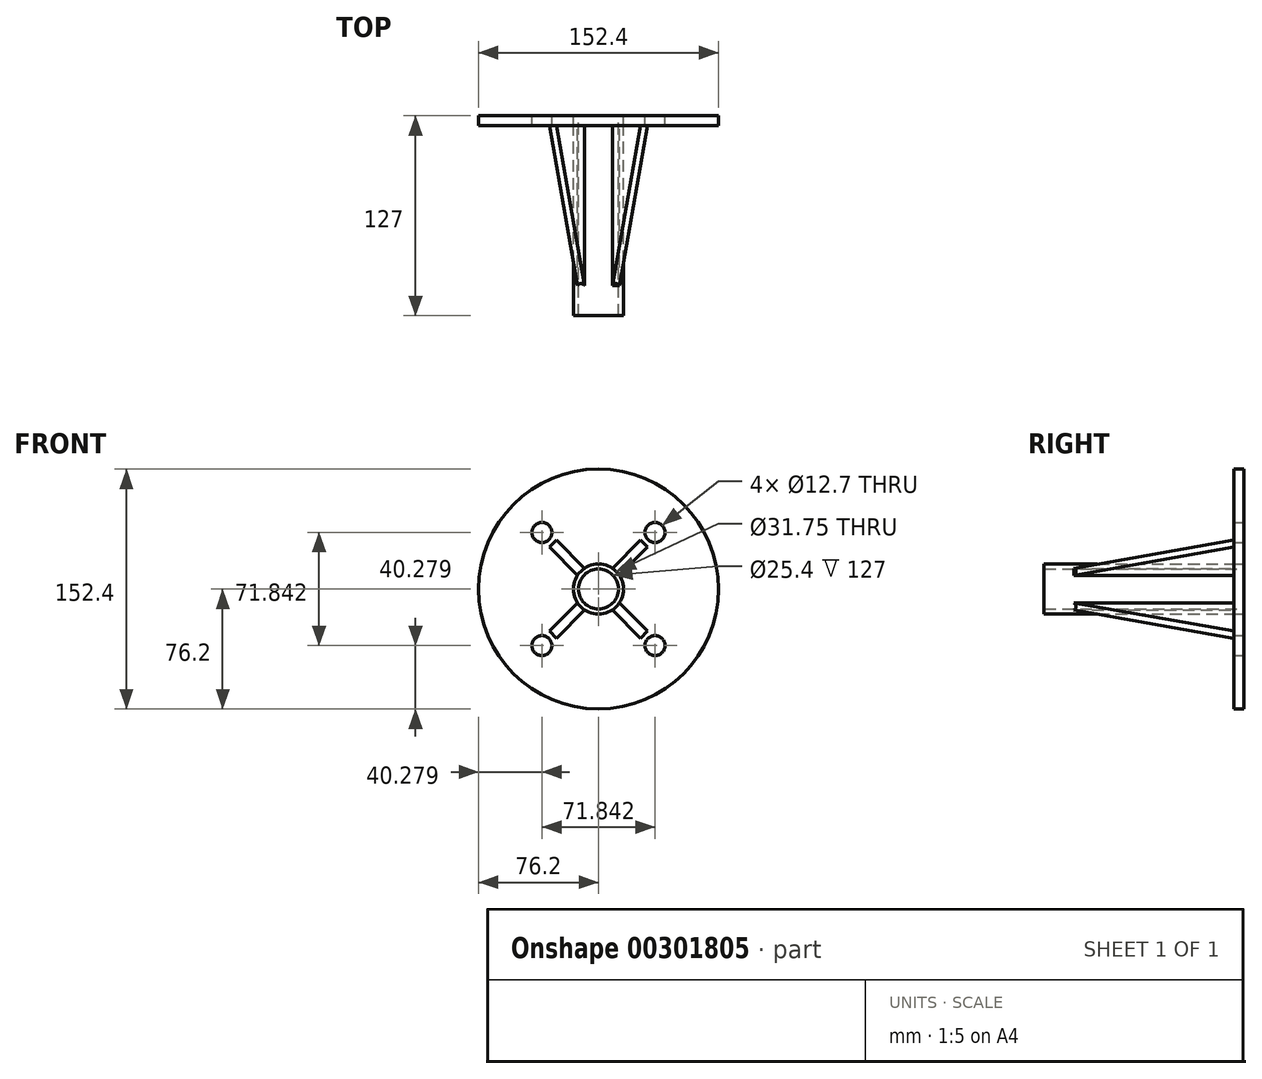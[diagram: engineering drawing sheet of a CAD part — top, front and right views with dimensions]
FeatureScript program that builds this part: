
annotation { "Feature Type Name" : "Feature", "Feature Type Description" : "" }
export const myFeature = defineFeature(function(context is Context, id is Id, definition is map)
    precondition{}
    {
        {
            var Q0;
            Q0=qCreatedBy(makeId("Front.planeOp"),FACE);
            var sketch = newSketch(context, id + "F0", { "sketchPlane" : qUnion([Q0])});
            skCircle(sketch, "E0", {"center": v(0, 0) * mm, "radius": 12.7 * mm});
            skCircle(sketch, "E1", {"center": v(0, 0) * mm, "radius": 15.88 * mm});
            skSolve(sketch);
        }
        {
            var Q0;
            Q0=makeQuery(id+"F0.imprint","IMPRINT",FACE,{"disambiguationData":[TD([[makeQuery(id+"F0.imprint","IMPRINT",EDGE,{"derivedFrom":sQuery(id+"F0.wireOp",EDGE,"E0")}),-1.0]])]});
            extrude(context, id + "F1", {"entities" : qUnion([Q0]), "depth" : 127 * mm});
        }
        {
            var Q0;
            Q0=qCreatedBy(makeId("Front.planeOp"),FACE);
            var sketch = newSketch(context, id + "F2", { "sketchPlane" : qUnion([Q0])});
            skCircle(sketch, "E2", {"center": v(0, 0) * mm, "radius": 15.88 * mm});
            skCircle(sketch, "E3", {"center": v(0, 0) * mm, "radius": 76.2 * mm});
            skCircle(sketch, "E4", {"center": v(-35.92, 35.92) * mm, "radius": 6.35 * mm});
            skLineSegment(sketch, "E5", {"start": v(0, -180.48) * mm, "end": v(0, 180.48) * mm, "construction": true});
            skLineSegment(sketch, "E6", {"start": v(169.83, 0) * mm, "end": v(-169.83, 0) * mm, "construction": true});
            skCircle(sketch, "E7.MirrorC", {"center": v(35.92, 35.92) * mm, "radius": 6.35 * mm});
            skCircle(sketch, "E8.MirrorC", {"center": v(-35.92, -35.92) * mm, "radius": 6.35 * mm});
            skCircle(sketch, "E9.MirrorC", {"center": v(35.92, -35.92) * mm, "radius": 6.35 * mm});
            skLineSegment(sketch, "E10", {"start": v(0, 0) * mm, "end": v(-35.92, 35.92) * mm, "construction": true});
            skSolve(sketch);
        }
        {
            var Q0;
            Q0=makeQuery(id+"F2.imprint","IMPRINT",FACE,{"disambiguationData":[TD([[makeQuery(id+"F2.imprint","IMPRINT",EDGE,{"derivedFrom":sQuery(id+"F2.wireOp",EDGE,"E2")}),-1.0]])]});
            extrude(context, id + "F3", {"entities" : qUnion([Q0]), "depth" : 6.35 * mm});
        }
        {
            var Q0;
            Q0=makeQuery(id+"F3.opExtrude","CAP_FACE",FACE,{"disambiguationData":[OSD([sQuery(id+"F2.wireOp",EDGE,"E2"),sQuery(id+"F2.wireOp",EDGE,"E3"),sQuery(id+"F2.wireOp",EDGE,"E4"),sQuery(id+"F2.wireOp",EDGE,"E7.MirrorC"),sQuery(id+"F2.wireOp",EDGE,"E8.MirrorC"),sQuery(id+"F2.wireOp",EDGE,"E9.MirrorC")])],"isStart":false});
            cPlane(context, id + "F4", {"entities" : qUnion([Q0]), "cplaneType" : CPlaneType.OFFSET, "offset" : 0 * mm, "width" : 152.4 * mm, "height" : 152.4 * mm});
        }
        {
            var Q0;
            Q0=qCreatedBy(id+"F4.planeOp",FACE);
            var sketch = newSketch(context, id + "F5", { "sketchPlane" : qUnion([Q0])});
            skCircle(sketch, "E11.0", {"center": v(0, 0) * mm, "radius": 15.88 * mm});
            skLineSegment(sketch, "E12", {"start": v(8.75, 13.24) * mm, "end": v(26.71, 31.2) * mm});
            skLineSegment(sketch, "E13", {"start": v(26.71, 31.2) * mm, "end": v(31.2, 26.71) * mm});
            skLineSegment(sketch, "E14", {"start": v(31.2, 26.71) * mm, "end": v(13.24, 8.75) * mm});
            skPoint(sketch, "E15", {"position": v(28.96, 28.96) * mm});
            skCircle(sketch, "E16.0", {"center": v(35.92, 35.92) * mm, "radius": 6.35 * mm});
            skLineSegment(sketch, "E17", {"start": v(35.92, 35.92) * mm, "end": v(28.96, 28.96) * mm, "construction": true});
            skLineSegment(sketch, "E18", {"start": v(-77.13, 0) * mm, "end": v(76.33, 0) * mm, "construction": true});
            skLineSegment(sketch, "E19", {"start": v(0, 76.18) * mm, "end": v(0, -52.75) * mm, "construction": true});
            skCircle(sketch, "E20.0.0", {"center": v(0, 0) * mm, "radius": 76.2 * mm});
            skLineSegment(sketch, "E21.MirrorCS", {"start": v(-8.75, 13.24) * mm, "end": v(-26.71, 31.2) * mm});
            skLineSegment(sketch, "E22.MirrorCS", {"start": v(-31.2, 26.71) * mm, "end": v(-13.24, 8.75) * mm});
            skLineSegment(sketch, "E23.MirrorCS", {"start": v(-26.71, 31.2) * mm, "end": v(-31.2, 26.71) * mm});
            skLineSegment(sketch, "E24.MirrorCS", {"start": v(31.2, -26.71) * mm, "end": v(13.24, -8.75) * mm});
            skLineSegment(sketch, "E25.MirrorCS", {"start": v(8.75, -13.24) * mm, "end": v(26.71, -31.2) * mm});
            skLineSegment(sketch, "E26.MirrorCS", {"start": v(26.71, -31.2) * mm, "end": v(31.2, -26.71) * mm});
            skLineSegment(sketch, "E27.MirrorCS", {"start": v(-26.71, -31.2) * mm, "end": v(-31.2, -26.71) * mm});
            skLineSegment(sketch, "E28.MirrorCS", {"start": v(-31.2, -26.71) * mm, "end": v(-13.24, -8.75) * mm});
            skLineSegment(sketch, "E29.MirrorCS", {"start": v(-8.75, -13.24) * mm, "end": v(-26.71, -31.2) * mm});
            skSolve(sketch);
        }
        {
            var Q0;
            {var subQ0=sQuery(id+"F5.wireOp",EDGE,"E12");Q0=makeQuery(id+"F5.imprint","IMPRINT",FACE,{"disambiguationData":[TD([[makeQuery(id+"F5.imprint","IMPRINT",EDGE,{"derivedFrom":subQ0}),-1.0]])]});}
            extrude(context, id + "F6", {"entities" : qUnion([Q0]), "depth" : 101.6 * mm});
        }
        {
            var Q0;
            Q0=makeQuery(id+"F6.opExtrude","SWEPT_FACE",FACE,{"disambiguationData":[OSD([sQuery(id+"F5.wireOp",EDGE,"E14")])]});
            var sketch = newSketch(context, id + "F7", { "sketchPlane" : qUnion([Q0])});
            skLineSegment(sketch, "E30.0.0", {"start": v(-6.35, 15.55) * mm, "end": v(-6.35, 40.95) * mm});
            skLineSegment(sketch, "E30.0.1", {"start": v(-6.35, 40.95) * mm, "end": v(-107.95, 40.95) * mm});
            skLineSegment(sketch, "E30.0.2", {"start": v(-107.95, 40.95) * mm, "end": v(-107.95, 15.55) * mm});
            skLineSegment(sketch, "E30.0.3", {"start": v(-107.95, 15.55) * mm, "end": v(-6.35, 15.55) * mm});
            skLineSegment(sketch, "E31", {"start": v(-107.95, 15.55) * mm, "end": v(-6.35, 40.95) * mm});
            skSolve(sketch);
        }
        {
            var Q0;
            Q0=makeQuery(id+"F7.imprint","IMPRINT",FACE,{"disambiguationData":[TD([[makeQuery(id+"F7.imprint","IMPRINT",EDGE,{"derivedFrom":sQuery(id+"F7.wireOp",EDGE,"E30.0.1")}),-1.0]])]});
            extrude(context, id + "F8", {"entities" : qUnion([Q0]), "operationType" : NewBodyOperationType.REMOVE, "endBound" : BoundingType.THROUGH_ALL, "oppositeDirection" : true, "depth" : 25.4 * mm});
        }
        {
            var Q0;
            Q0=qCreatedBy(makeId("Top.planeOp"),FACE);
            var sketch = newSketch(context, id + "F9", { "sketchPlane" : qUnion([Q0])});
            skLineSegment(sketch, "E32", {"start": v(0, 0) * mm, "end": v(0, -155.97) * mm, "construction": true});
            skSolve(sketch);
        }
        {
            var Q0;
            Q0=makeQuery(id+"F6.opExtrude","SWEPT_BODY",BODY,{"disambiguationData":[OSD([sQuery(id+"F5.wireOp",EDGE,"E12"),sQuery(id+"F5.wireOp",EDGE,"E13"),sQuery(id+"F5.wireOp",EDGE,"E14"),sQuery(id+"F5.wireOp",EDGE,"E11.0")])]});
            var Q1;
            Q1=sQuery(id+"F9.wireOp",EDGE,"E32");
            circularPattern(context, id + "F10", {"entities" : qUnion([Q0]), "axis" : qUnion([Q1]), "angle" : 360 * degree, "instanceCount" : 4, "equalSpace" : true});
        }
    });
